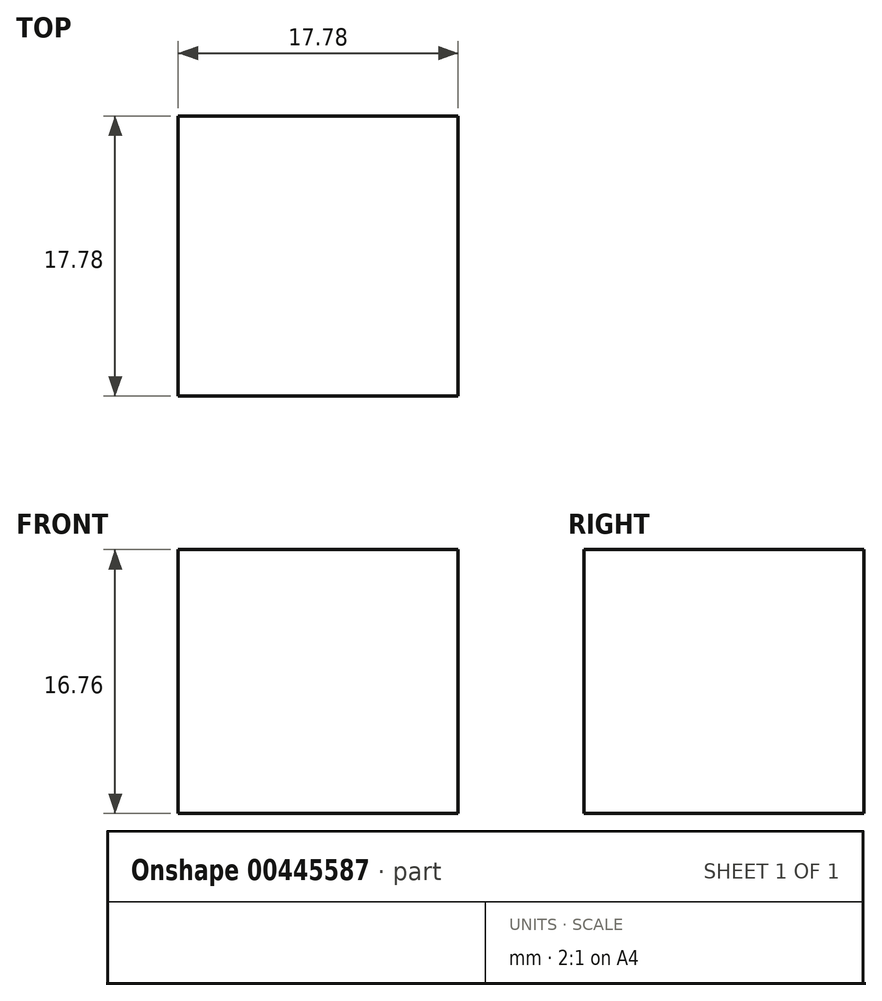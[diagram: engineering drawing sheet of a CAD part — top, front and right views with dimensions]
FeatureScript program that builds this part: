
annotation { "Feature Type Name" : "Feature", "Feature Type Description" : "" }
export const myFeature = defineFeature(function(context is Context, id is Id, definition is map)
    precondition{}
    {
        {
            var Q0;
            Q0=qCreatedBy(makeId("Top.planeOp"),FACE);
            var sketch = newSketch(context, id + "F0", { "sketchPlane" : qUnion([Q0])});
            skLineSegment(sketch, "E0.bottom", {"start": v(-25.4, 29.94) * mm, "end": v(-7.61, 29.94) * mm});
            skLineSegment(sketch, "E0.top", {"start": v(-25.4, 12.16) * mm, "end": v(-7.61, 12.16) * mm});
            skLineSegment(sketch, "E0.left", {"start": v(-25.4, 29.94) * mm, "end": v(-25.4, 12.16) * mm});
            skLineSegment(sketch, "E0.right", {"start": v(-7.61, 29.94) * mm, "end": v(-7.61, 12.16) * mm});
            skSolve(sketch);
        }
        {
            var Q0;
            Q0 = qSketchRegion(id + "F0", true);
            extrude(context, id + "F1", {"entities" : qUnion([Q0]), "depth" : 16.76 * mm});
        }
    });
